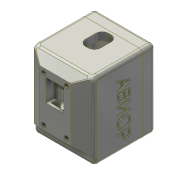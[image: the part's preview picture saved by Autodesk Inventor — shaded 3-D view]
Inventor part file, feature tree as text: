
AUTODESK INVENTOR PART (.ipt)
format: ipt  version: 2021 (Build 250183000, 183)  size: 880,640 bytes
history: native  units: mm
features: extrude x15, sketch x15, projected_geometry x15, other x6, fillet x5, hole x5, shell x1, loft x1, mirror x1
ambient origin geometry x8: Origin, YZ Plane, XZ Plane, XY Plane, X Axis, Y Axis, Z Axis, Center Point
bodies: Body1 (feature_tree), Body2 (feature_tree)
feature tree (64):
  other  "Твердое тело1"
  extrude  "Выдавливание1"  Depth=42.0mm
  shell  "Оболочка1"  Thickness=55.0mm
  other  "РабПлоскость1"
  extrude  "Выдавливание25"  Depth=3.0mm
  extrude  "Выдавливание26"  [1 undecoded]
  other  "Разделение1"
  other  "РабПлоскость2"
  loft  "Лофт1"
  extrude  "Выдавливание4"  Depth=15.5mm
  extrude  "Выдавливание7"  Depth=12.0mm
  fillet  "Сопряжение9"  [1 undecoded]
  hole  "Отверстие2"  [1 undecoded]
  mirror  "Зеркальное отражение1"
  fillet  "Сопряжение10"  Radius=25.0mm
  extrude  "Выдавливание8"  Depth=6.0mm
  hole  "Отверстие7"  [1 undecoded]
  extrude  "Выдавливание22"  Depth=14.0mm
  extrude  "Выдавливание27"  Depth=6.5mm TaperAngle=0.0deg
  extrude  "Выдавливание28"  Depth=14.0mm
  extrude  "Выдавливание11"  Depth=2.0mm
  extrude  "Выдавливание12"  Depth=3.9mm
  hole  "Отверстие1"  [1 undecoded]
  fillet  "Сопряжение14"  Radius=9.899495mm
  fillet  "Сопряжение15"  Radius=4.0mm
  sketch  "Эскиз21"
  extrude  "Выдавливание15"  Depth=2.0mm
  hole  "Отверстие4"  [1 undecoded]
  hole  "Отверстие5"  [1 undecoded]
  extrude  "Выдавливание19"  Depth=1.5mm
  extrude  "Выдавливание20"  Depth=10.12mm
  fillet  "Сопряжение17"  Radius=18.0mm
  extrude  "Выдавливание21"  Depth=4.0mm TaperAngle=0.0deg
  sketch  "Эскиз1"
  sketch  "Эскиз3"
  projected_geometry  "Спроецированная петля2"
  sketch  "Эскиз4"
  sketch  "Эскиз6"
  projected_geometry  "Спроецированная петля4"
  projected_geometry  "Спроецированная петля5"
  projected_geometry  "Спроецированная петля8"
  projected_geometry  "Спроецированная петля9"
  projected_geometry  "Спроецированная петля10"
  projected_geometry  "Спроецированная петля11"
  projected_geometry  "Спроецированная петля14"
  projected_geometry  "Спроецированная петля15"
  sketch  "Эскиз30"
  projected_geometry  "Спроецированная петля17"
  sketch  "Эскиз36"
  sketch  "Эскиз37"
  sketch  "Эскиз39"
  sketch  "Эскиз40"
  projected_geometry  "Спроецированная петля20"
  sketch  "Эскиз45"
  projected_geometry  "Спроецированная петля22"
  sketch  "Эскиз48"
  projected_geometry  "Спроецированная петля26"
  sketch  "Эскиз49"
  projected_geometry  "Спроецированная петля27"
  sketch  "Эскиз50"
  projected_geometry  "Спроецированная петля30"
  sketch  "Эскиз51"
  other  "Твердое тело2"
  other  "Твердое тело3"
note: 7 required parameter values undecoded (feature->parameter linkage not recoverable at this tier; creation-order binding heuristic only, values carry confidence <= 0.55)
